# Revit family: 306_edf39f34e9d74d9bafc467eac0d58d
name_source: partatom
category: Pipe Accessories
units: mm (PartAtom-declared; Revit-internal decimal feet)

## family parameters
Always vertical = Yes
Cut with Voids When Loaded = No
Part Type = Valve - Breaks Into
Round Connector Dimension = Use Diameter
Shared = No
Work Plane-Based = No

## types (5) — shared parameters
Description = 3-way Control valve VLB335, PN16 flange
L2D = 350 mm
L2D_Min = 3048 mm
MC = No
Manufacturer = ESBE
QmdConnectorList = 301;D;302;D
R9 = 4 mm  [stored 0.0131234 ft]
URL = http://www.esbe.eu
W2D = 100 mm
X1 = 2 mm  [stored 0.00656168 ft]
Z10 = 5 mm  [stored 0.0164042 ft]
Z19 = 10 mm  [stored 0.0328084 ft]
Z4 = 12 mm  [stored 0.0393701 ft]
Z5 = 6 mm  [stored 0.019685 ft]
Z6 = 6 mm  [stored 0.019685 ft]
Z7 = 3 mm  [stored 0.00984252 ft]
Z8 = 6 mm  [stored 0.019685 ft]
Z9 = 4 mm  [stored 0.0131234 ft]
magiPartTypeId = 306
magiProductFamilyId = edf39f34e9d74d9bafc467eac0d58d

## per-type parameters (varying)
- VLB335 PN16 FLANGE DN100 Kvs130: CenSd_R6_6=15 mm  [stored 0.0492126 ft]; D=100 mm; D2=69 mm; D3=81 mm; D4=69 mm; FDT2=110 mm; H2=45 mm; H3=117 mm; H4=175 mm; HCDT2=77 mm; LT2=175 mm; R1=46 mm; R12=5 mm  [stored 0.0164042 ft]; R13=55 mm; R2=57 mm; R3=31 mm; R4=25 mm  [stored 0.082021 ft]; R5=20 mm  [stored 0.0656168 ft]; R6=17 mm; R7=10 mm  [stored 0.0328084 ft]; X2=17 mm; X2__ve=-17 mm; X4=17 mm; Z12=55 mm; Z13=8 mm  [stored 0.0262467 ft]; Z14=15 mm  [stored 0.0492126 ft]; Z14__ve=-15 mm; Z15=41 mm; Z3=166 mm; magiProductId=e8a338e699cd440aacf2ace103e92c
- VLB335 PN16 FLANGE DN125 Kvs200: CenSd_R6_6=17 mm; D=125 mm; D2=79 mm; D3=96 mm; D4=82 mm; FDT2=125 mm; H2=45 mm; H3=139 mm; H4=200 mm; HCDT2=92 mm; LT2=200 mm; R1=55 mm; R12=6 mm  [stored 0.019685 ft]; R13=66 mm; R2=69 mm; R3=36 mm; R4=29 mm; R5=23 mm; R6=19 mm; R7=12 mm  [stored 0.0393701 ft]; X2=20 mm  [stored 0.0656168 ft]; X2__ve=-20 mm  [stored -0.0656168 ft]; X4=20 mm  [stored 0.0656168 ft]; Z12=63 mm; Z13=9 mm  [stored 0.0295276 ft]; Z14=17 mm; Z14__ve=-17 mm; Z15=49 mm; Z3=194 mm; magiProductId=122af6610eb74de691aa6ccc943ec1
- VLB335 PN16 FLANGE DN150 Kvs300: CenSd_R6_6=20 mm  [stored 0.0656168 ft]; D=150 mm; D2=95 mm; D3=109 mm; D4=93 mm; FDT2=143 mm; H2=45 mm; H3=157 mm; H4=240 mm; HCDT2=104 mm; LT2=240 mm; R1=62 mm; R12=7 mm  [stored 0.0229659 ft]; R13=75 mm; R2=78 mm; R3=43 mm; R4=34 mm; R5=27 mm; R6=23 mm; R7=14 mm  [stored 0.0459318 ft]; X2=24 mm; X2__ve=-24 mm; X4=24 mm; Z12=76 mm; Z13=11 mm; Z14=20 mm  [stored 0.0656168 ft]; Z14__ve=-20 mm  [stored -0.0656168 ft]; Z15=55 mm; Z3=226 mm; magiProductId=296f00f0978845e0a8f3f6dbb409af
- VLB335 PN16 FLANGE DN65 Kvs63: CenSd_R6_6=12 mm  [stored 0.0393701 ft]; D=65 mm; D2=57 mm; D3=64 mm; D4=54 mm; FDT2=93 mm; H2=25 mm  [stored 0.082021 ft]; H3=95 mm; H4=145 mm; HCDT2=59 mm; LT2=145 mm; R1=35 mm; R12=4 mm  [stored 0.0131234 ft]; R13=42 mm; R2=44 mm; R3=26 mm; R4=21 mm; R5=16 mm; R6=14 mm  [stored 0.0459318 ft]; R7=8 mm  [stored 0.0262467 ft]; X2=14 mm  [stored 0.0459318 ft]; X2__ve=-14 mm; X4=14 mm  [stored 0.0459318 ft]; Z12=46 mm; Z13=7 mm  [stored 0.0229659 ft]; Z14=12 mm  [stored 0.0393701 ft]; Z14__ve=-12 mm; Z15=33 mm; Z3=137 mm; magiProductId=5aac43a2511d4165beb0913c2304e6
- VLB335 PN16 FLANGE DN80 Kvs100: CenSd_R6_6=13 mm; D=80 mm; D2=61 mm; D3=71 mm; D4=60 mm; FDT2=100 mm; H2=45 mm; H3=105 mm; H4=155 mm; HCDT2=67 mm; LT2=155 mm; R1=40 mm; R12=5 mm  [stored 0.0164042 ft]; R13=48 mm; R2=50 mm; R3=28 mm; R4=22 mm; R5=18 mm; R6=15 mm  [stored 0.0492126 ft]; R7=9 mm  [stored 0.0295276 ft]; X2=15 mm  [stored 0.0492126 ft]; X2__ve=-15 mm; X4=15 mm  [stored 0.0492126 ft]; Z12=49 mm; Z13=7 mm  [stored 0.0229659 ft]; Z14=13 mm; Z14__ve=-13 mm; Z15=37 mm; Z3=149 mm; magiProductId=0cc30eccbd804e85bfa24a58891dd5

note: column(s) folded — value = type name in every type: magiProductCode

note: [stored X ft] marks values corroborated as IEEE doubles in the binary element streams (Revit-internal decimal feet)

## geometry (parser evidence)
native form markers: Sweep x1
no freeform markers — native parametric forms only
